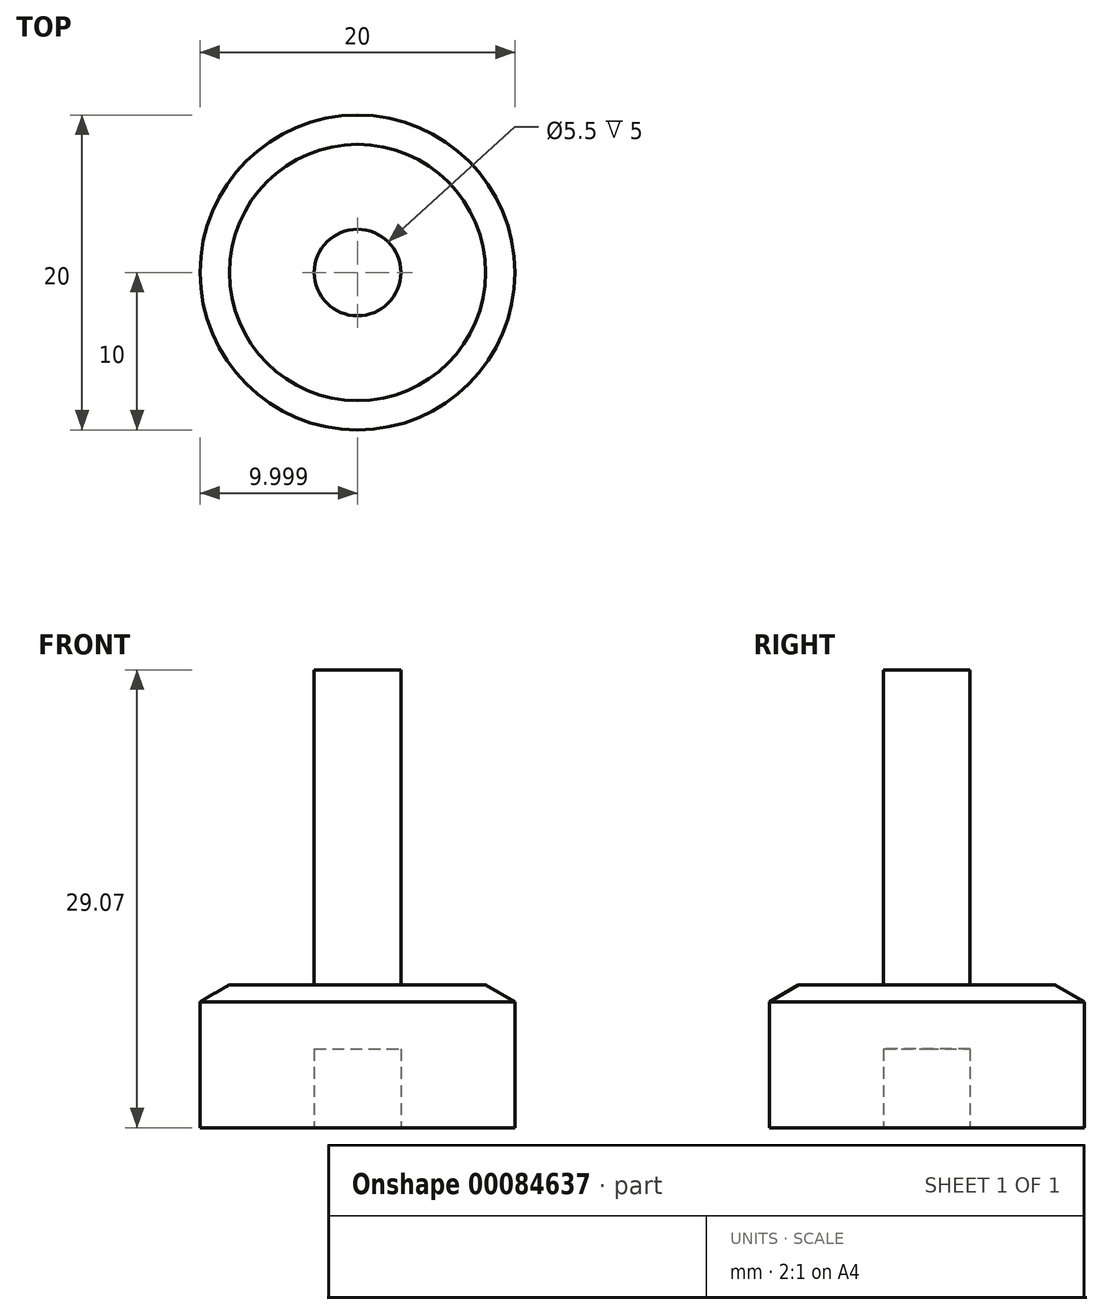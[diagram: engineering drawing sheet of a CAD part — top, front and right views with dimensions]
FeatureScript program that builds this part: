
annotation { "Feature Type Name" : "Feature", "Feature Type Description" : "" }
export const myFeature = defineFeature(function(context is Context, id is Id, definition is map)
    precondition{}
    {
        {
            var Q0;
            Q0=qCreatedBy(makeId("Front.planeOp"),FACE);
            var sketch = newSketch(context, id + "F0", { "sketchPlane" : qUnion([Q0])});
            skLineSegment(sketch, "E0.bottom", {"start": v(-30.55, 8) * mm, "end": v(-20.55, 8) * mm});
            skLineSegment(sketch, "E0.top", {"start": v(-30.55, 0) * mm, "end": v(-23.3, 0) * mm});
            skLineSegment(sketch, "E0.left", {"start": v(-30.55, 8) * mm, "end": v(-30.55, 0) * mm});
            skPoint(sketch, "E1", {"position": v(-20.55, 8) * mm});
            skPoint(sketch, "E2", {"position": v(-20.55, 0) * mm});
            skPoint(sketch, "E3", {"position": v(-20.55, 9.07) * mm});
            skLineSegment(sketch, "E4", {"start": v(-20.55, 8) * mm, "end": v(-20.55, 9.07) * mm});
            skLineSegment(sketch, "E5", {"start": v(-30.55, 8) * mm, "end": v(-28.7, 9.07) * mm});
            skLineSegment(sketch, "E6", {"start": v(-28.7, 9.07) * mm, "end": v(-20.55, 9.07) * mm});
            skLineSegment(sketch, "E7", {"start": v(-20.55, 8) * mm, "end": v(-20.55, 5) * mm});
            skPoint(sketch, "E0.right.end.orphan", {"position": v(-10.55, 0) * mm});
            skPoint(sketch, "E8.start.orphan", {"position": v(-10.55, 8) * mm});
            skLineSegment(sketch, "E9", {"start": v(-20.55, 9.07) * mm, "end": v(-20.55, 29.07) * mm});
            skLineSegment(sketch, "E10", {"start": v(-20.55, 29.07) * mm, "end": v(-23.3, 29.07) * mm});
            skLineSegment(sketch, "E11", {"start": v(-23.3, 29.07) * mm, "end": v(-23.3, 0) * mm});
            skPoint(sketch, "E12.start.orphan", {"position": v(-20.55, 4) * mm});
            skLineSegment(sketch, "E13", {"start": v(-20.55, 5) * mm, "end": v(-23.3, 5) * mm});
            skPoint(sketch, "E14", {"position": v(-20.55, 5) * mm});
            skSolve(sketch);
        }
        {
            var Q0;
            {var subQ0=sQuery(id+"F0.wireOp",EDGE,"E9");Q0=makeQuery(id+"F0.imprint","IMPRINT",FACE,{"disambiguationData":[TD([[makeQuery(id+"F0.imprint","IMPRINT",EDGE,{"derivedFrom":subQ0}),1.0]])]});}
            var Q1;
            {var subQ5=sQuery(id+"F0.wireOp",EDGE,"E0.top");Q1=makeQuery(id+"F0.imprint","IMPRINT",FACE,{"disambiguationData":[TD([[makeQuery(id+"F0.imprint","IMPRINT",EDGE,{"derivedFrom":subQ5}),1.0]])]});}
            var Q2;
            {var subQ0=sQuery(id+"F0.wireOp",EDGE,"E5");Q2=makeQuery(id+"F0.imprint","IMPRINT",FACE,{"disambiguationData":[TD([[makeQuery(id+"F0.imprint","IMPRINT",EDGE,{"derivedFrom":subQ0}),-1.0]])]});}
            var Q3;
            {var subQ0=sQuery(id+"F0.wireOp",EDGE,"E7");Q3=makeQuery(id+"F0.imprint","IMPRINT",FACE,{"disambiguationData":[TD([[makeQuery(id+"F0.imprint","IMPRINT",EDGE,{"derivedFrom":subQ0}),-1.0]])]});}
            var Q4;
            {var subQ0=sQuery(id+"F0.wireOp",EDGE,"E4");Q4=makeQuery(id+"F0.imprint","IMPRINT",FACE,{"disambiguationData":[TD([[makeQuery(id+"F0.imprint","IMPRINT",EDGE,{"derivedFrom":subQ0}),1.0]])]});}
            var Q5;
            Q5=sQuery(id+"F0.wireOp",EDGE,"E9");
            revolve(context, id + "F1", {"entities" : qUnion([Q0, Q1, Q2, Q3, Q4]), "axis" : qUnion([Q5]), "revolveType" : RevolveType.FULL});
        }
    });
